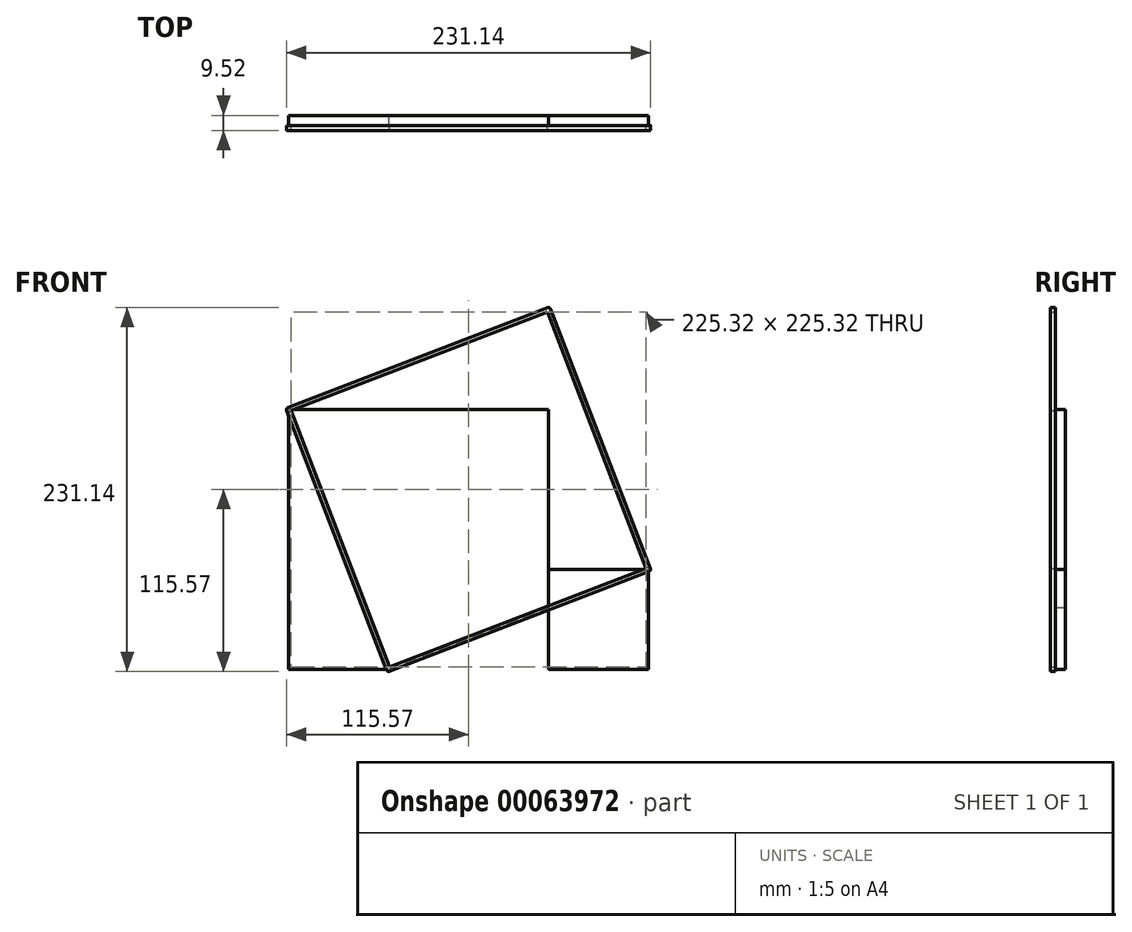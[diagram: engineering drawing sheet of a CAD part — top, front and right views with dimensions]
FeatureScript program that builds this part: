
annotation { "Feature Type Name" : "Feature", "Feature Type Description" : "" }
export const myFeature = defineFeature(function(context is Context, id is Id, definition is map)
    precondition{}
    {
        {
            var Q0;
            Q0=qCreatedBy(makeId("Front.planeOp"),FACE);
            var sketch = newSketch(context, id + "F0", { "sketchPlane" : qUnion([Q0])});
            skLineSegment(sketch, "E0.rect.bottom", {"start": v(82.55, 82.55) * mm, "end": v(-82.55, 82.55) * mm});
            skLineSegment(sketch, "E0.rect.top", {"start": v(82.55, -82.55) * mm, "end": v(-82.55, -82.55) * mm});
            skLineSegment(sketch, "E0.rect.left", {"start": v(82.55, 82.55) * mm, "end": v(82.55, -82.55) * mm});
            skLineSegment(sketch, "E0.rect.right", {"start": v(-82.55, 82.55) * mm, "end": v(-82.55, -82.55) * mm});
            skPoint(sketch, "E0.rect.middle", {"position": v(0, 0) * mm});
            skLineSegment(sketch, "E1.rect.bottom", {"start": v(82.55, -82.55) * mm, "end": v(146.05, -82.55) * mm});
            skLineSegment(sketch, "E1.rect.top", {"start": v(82.55, -19.05) * mm, "end": v(146.05, -19.05) * mm});
            skLineSegment(sketch, "E1.rect.left", {"start": v(82.55, -82.55) * mm, "end": v(82.55, -19.05) * mm});
            skLineSegment(sketch, "E1.rect.right", {"start": v(146.05, -82.55) * mm, "end": v(146.05, -19.05) * mm});
            skPoint(sketch, "E1.rect.middle", {"position": v(114.3, -50.8) * mm});
            skLineSegment(sketch, "E2", {"start": v(-82.55, 82.55) * mm, "end": v(-19.05, -82.55) * mm});
            skLineSegment(sketch, "E3", {"start": v(-19.05, -82.55) * mm, "end": v(146.05, -19.05) * mm});
            skLineSegment(sketch, "E4", {"start": v(-82.55, 82.55) * mm, "end": v(82.55, 146.05) * mm});
            skLineSegment(sketch, "E5", {"start": v(82.55, 146.05) * mm, "end": v(146.05, -19.05) * mm});
            skLineSegment(sketch, "E6.1.0.0", {"start": v(146.05, -19.05) * mm, "end": v(311.15, 44.45) * mm});
            skLineSegment(sketch, "E6.1.0.2", {"start": v(82.55, 146.05) * mm, "end": v(247.65, 209.55) * mm});
            skLineSegment(sketch, "E6.1.0.3", {"start": v(247.65, 209.55) * mm, "end": v(311.15, 44.45) * mm});
            skLineSegment(sketch, "E6.2.0.0", {"start": v(311.15, 44.45) * mm, "end": v(476.25, 107.95) * mm});
            skLineSegment(sketch, "E6.2.0.1", {"start": v(247.65, 209.55) * mm, "end": v(311.15, 44.45) * mm});
            skLineSegment(sketch, "E6.2.0.2", {"start": v(247.65, 209.55) * mm, "end": v(412.75, 273.05) * mm});
            skLineSegment(sketch, "E6.2.0.3", {"start": v(412.75, 273.05) * mm, "end": v(476.25, 107.95) * mm});
            skLineSegment(sketch, "E6.direction1", {"start": v(-19.05, -82.55) * mm, "end": v(146.05, -19.05) * mm, "construction": true});
            skLineSegment(sketch, "E7.1.0.0", {"start": v(-146.05, 247.65) * mm, "end": v(-82.55, 82.55) * mm});
            skLineSegment(sketch, "E7.1.0.1", {"start": v(-146.05, 247.65) * mm, "end": v(19.05, 311.15) * mm});
            skLineSegment(sketch, "E7.1.0.2", {"start": v(19.05, 311.15) * mm, "end": v(82.55, 146.05) * mm});
            skLineSegment(sketch, "E7.1.0.4", {"start": v(19.05, 311.15) * mm, "end": v(184.15, 374.65) * mm});
            skLineSegment(sketch, "E7.1.0.6", {"start": v(184.15, 374.65) * mm, "end": v(247.65, 209.55) * mm});
            skLineSegment(sketch, "E7.1.0.7", {"start": v(184.15, 374.65) * mm, "end": v(349.25, 438.15) * mm});
            skLineSegment(sketch, "E7.1.0.9", {"start": v(349.25, 438.15) * mm, "end": v(412.75, 273.05) * mm});
            skLineSegment(sketch, "E7.2.0.0", {"start": v(-209.55, 412.75) * mm, "end": v(-146.05, 247.65) * mm});
            skLineSegment(sketch, "E7.2.0.1", {"start": v(-209.55, 412.75) * mm, "end": v(-44.45, 476.25) * mm});
            skLineSegment(sketch, "E7.2.0.2", {"start": v(-44.45, 476.25) * mm, "end": v(19.05, 311.15) * mm});
            skLineSegment(sketch, "E7.2.0.3", {"start": v(-146.05, 247.65) * mm, "end": v(19.05, 311.15) * mm});
            skLineSegment(sketch, "E7.2.0.4", {"start": v(-44.45, 476.25) * mm, "end": v(120.65, 539.75) * mm});
            skLineSegment(sketch, "E7.2.0.5", {"start": v(19.05, 311.15) * mm, "end": v(184.15, 374.65) * mm});
            skLineSegment(sketch, "E7.2.0.6", {"start": v(120.65, 539.75) * mm, "end": v(184.15, 374.65) * mm});
            skLineSegment(sketch, "E7.2.0.7", {"start": v(120.65, 539.75) * mm, "end": v(285.75, 603.25) * mm});
            skLineSegment(sketch, "E7.2.0.8", {"start": v(184.15, 374.65) * mm, "end": v(349.25, 438.15) * mm});
            skLineSegment(sketch, "E7.2.0.9", {"start": v(285.75, 603.25) * mm, "end": v(349.25, 438.15) * mm});
            skLineSegment(sketch, "E7.direction1", {"start": v(-19.05, -82.55) * mm, "end": v(-82.55, 82.55) * mm, "construction": true});
            skSolve(sketch);
        }
        {
            var Q0;
            {var subQ0=sQuery(id+"F0.wireOp",EDGE,"E0.rect.right");Q0=makeQuery(id+"F0.imprint","IMPRINT",FACE,{"disambiguationData":[TD([[makeQuery(id+"F0.imprint","IMPRINT",EDGE,{"derivedFrom":subQ0}),1.0]])]});}
            var Q1;
            Q1=makeQuery(id+"F0.imprint","IMPRINT",FACE,{"disambiguationData":[TD([[makeQuery(id+"F0.imprint","IMPRINT",EDGE,{"derivedFrom":sQuery(id+"F0.wireOp",EDGE,"E0.rect.bottom")}),1.0]])]});
            var Q2;
            {var subQ0=sQuery(id+"F0.wireOp",EDGE,"E1.rect.left");var subQ3=sQuery(id+"F0.wireOp",EDGE,"E3");var subQ5=makeQuery(id+"F0.imprint","INTERSECT",VERTEX,{"derivedFrom":[subQ0,subQ3]});Q2=makeQuery(id+"F0.imprint","IMPRINT",FACE,{"disambiguationData":[TD([[makeQuery(id+"F0.imprint","IMPRINT",EDGE,{"disambiguationData":[TD([[subQ5,1.0]])],"derivedFrom":subQ0}),1.0]])]});}
            extrude(context, id + "F1", {"entities" : qUnion([Q0, Q1, Q2]), "oppositeDirection" : true, "depth" : 6.35 * mm});
        }
        {
            var Q0;
            {var subQ0=sQuery(id+"F0.wireOp",EDGE,"E1.rect.bottom");Q0=makeQuery(id+"F0.imprint","IMPRINT",FACE,{"disambiguationData":[TD([[makeQuery(id+"F0.imprint","IMPRINT",EDGE,{"derivedFrom":subQ0}),1.0]])]});}
            var Q1;
            {var subQ0=sQuery(id+"F0.wireOp",EDGE,"E1.rect.top");Q1=makeQuery(id+"F0.imprint","IMPRINT",FACE,{"disambiguationData":[TD([[makeQuery(id+"F0.imprint","IMPRINT",EDGE,{"derivedFrom":subQ0}),-1.0]])]});}
            extrude(context, id + "F2", {"entities" : qUnion([Q0, Q1]), "oppositeDirection" : true, "depth" : 6.35 * mm});
        }
        {
            var Q0;
            Q0=qCreatedBy(makeId("Front.planeOp"),FACE);
            var sketch = newSketch(context, id + "F3", { "sketchPlane" : qUnion([Q0])});
            skLineSegment(sketch, "E8.JFh.JFh", {"start": v(-82.55, 82.55) * mm, "end": v(-19.05, -82.55) * mm, "construction": true});
            skLineSegment(sketch, "E8.KFhB.KFhB", {"start": v(-82.55, 82.55) * mm, "end": v(82.55, 146.05) * mm, "construction": true});
            skLineSegment(sketch, "E8.JFt.JFt", {"start": v(82.55, 146.05) * mm, "end": v(146.05, -19.05) * mm, "construction": true});
            skLineSegment(sketch, "E8.JFl.JFl", {"start": v(-19.05, -82.55) * mm, "end": v(146.05, -19.05) * mm, "construction": true});
            skArc(sketch, "E8.0.startCap", {"start": v(-83.74, 82.1) * mm, "mid": v(-83, 83.74) * mm, "end": v(-81.36, 83) * mm});
            skArc(sketch, "E8.0.endCap", {"start": v(-17.86, -82.1) * mm, "mid": v(-18.6, -83.74) * mm, "end": v(-20.24, -83) * mm});
            skLineSegment(sketch, "E8.0.left", {"start": v(-81.36, 83) * mm, "end": v(-17.86, -82.1) * mm});
            skLineSegment(sketch, "E8.0.right", {"start": v(-83.74, 82.1) * mm, "end": v(-20.24, -83) * mm});
            skArc(sketch, "E8.1.startCap", {"start": v(-82.1, 81.36) * mm, "mid": v(-83.74, 82.1) * mm, "end": v(-83, 83.74) * mm});
            skArc(sketch, "E8.1.endCap", {"start": v(82.1, 147.24) * mm, "mid": v(83.74, 146.5) * mm, "end": v(83, 144.86) * mm});
            skLineSegment(sketch, "E8.1.left", {"start": v(-83, 83.74) * mm, "end": v(82.1, 147.24) * mm});
            skLineSegment(sketch, "E8.1.right", {"start": v(-82.1, 81.36) * mm, "end": v(83, 144.86) * mm});
            skArc(sketch, "E8.2.startCap", {"start": v(81.36, 145.6) * mm, "mid": v(82.1, 147.24) * mm, "end": v(83.74, 146.5) * mm});
            skArc(sketch, "E8.2.endCap", {"start": v(147.24, -18.6) * mm, "mid": v(146.5, -20.24) * mm, "end": v(144.86, -19.5) * mm});
            skLineSegment(sketch, "E8.2.left", {"start": v(83.74, 146.5) * mm, "end": v(147.24, -18.6) * mm});
            skLineSegment(sketch, "E8.2.right", {"start": v(81.36, 145.6) * mm, "end": v(144.86, -19.5) * mm});
            skArc(sketch, "E8.3.startCap", {"start": v(-18.6, -83.74) * mm, "mid": v(-20.24, -83) * mm, "end": v(-19.5, -81.36) * mm});
            skArc(sketch, "E8.3.endCap", {"start": v(145.6, -17.86) * mm, "mid": v(147.24, -18.6) * mm, "end": v(146.5, -20.24) * mm});
            skLineSegment(sketch, "E8.3.left", {"start": v(-19.5, -81.36) * mm, "end": v(145.6, -17.86) * mm});
            skLineSegment(sketch, "E8.3.right", {"start": v(-18.6, -83.74) * mm, "end": v(146.5, -20.24) * mm});
            skSolve(sketch);
        }
        {
            var Q0;
            Q0 = qSketchRegion(id + "F3", true);
            extrude(context, id + "F4", {"entities" : qUnion([Q0]), "depth" : 3.17 * mm});
        }
    });
